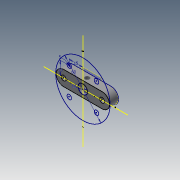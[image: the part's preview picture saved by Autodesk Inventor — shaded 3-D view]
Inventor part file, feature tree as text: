
AUTODESK INVENTOR PART (.ipt)
format: ipt  version: 2015 (Build 190159000, 159)  size: 135,680 bytes
history: native  units: mm
features: other x7, sketch x4, extrude x2, plane x1, projected_geometry x1
ambient origin geometry x8: Origin, YZ Plane, XZ Plane, XY Plane, X Axis, Y Axis, Z Axis, Center Point
bodies: Body1 (feature_tree)
feature tree (15):
  other  "Blocks"
  sketch  "Sketch1"  dims[d0=60.0mm d1=20.0mm]
  plane  "Work Plane1"
  extrude  "Extrusion4"  Depth=20.0mm
  extrude  "Extrusion5"  Depth=10.0mm
  sketch  "Sketch8"  dims[d32=15.0mm d33=15.0mm d36=8.0mm d37=5.0mm d38=5.0mm d39=42.426407mm d40=10.0mm d41=10.0mm d42=0.0mm d43=5.0mm d44=5.0mm d45=21.213203mm d46=10.0mm d47=0.0mm]
  other  "DXF"
  other  "Block1"
  other  "Block2"
  sketch  "Sketch6"  dims[d7=10.0mm d8=40.0mm]
  sketch  "Sketch7"  dims[d31=5.0mm]
  projected_geometry  "Projected Loop2"
  other  "Block3"
  other  "Block3:1"
  other  "Block3:2"
